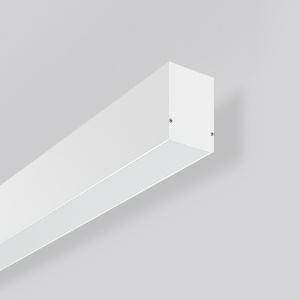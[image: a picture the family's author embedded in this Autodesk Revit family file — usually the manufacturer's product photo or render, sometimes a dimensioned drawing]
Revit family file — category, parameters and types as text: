
# Revit family: less_is_more_50_312606_002_e624
name_source: partatom
category: Lighting Fixtures
units: mm (PartAtom-declared; Revit-internal decimal feet)

## family parameters
Cut with Voids When Loaded = No
Host = Face
Light Source = No
Part Type = Normal
Room Calculation Point = No
Round Connector Dimension = Use Diameter
Shared = No

## types (1)
- LESS IS MORE 50 (1 x LED Modul 830, 1950 lm, 3000)
    Apparent Load = 15 VA
    CIE Flux Codes = 48 80 96 50 100
    Color Rendering = 80
    Color Temperature = 3000
    Default Elevation = 1800 mm
    Description = Series: LESS IS MORE 50
Linear wall luminaires. Housing: extruded aluminium profile, powder-coated. End cap aluminium powder-coated. Diffuser made of non-yellowing plastic (PMMA), opal. Direct 50%, indirect 50% light emission. Suitable for Wall (surface). LED unit with integrated converter interchangeable and removable. Suitable for through-wiring. With sensors or as a safety luminaire on request. 
Colour: traffic white, matt (RAL 9016)
Length: 847 mm
Width: 67 mm
Height: 75 mm
Lamp: LED
Socket: without socket
Colour temperature: 3000K
Colour rendering index (CRI): 80
Light source: LED
Socket lamp2: Without base
Colour temperature: 3000K
Colour rendering index (CRI) 2: 80
System power: 15 W
Rated luminous flux: 1950 lm
Luminous efficiency: 130 lm/W
Control gear: Regulated power supply
Control gear: Regulated power supply
Protection class: I
Type of protection: IP 20
    Height = 75 mm
    Lamp = 1 x LED Modul 830
    Lamp Light Flux = 1950 lm
    Lamp count = 1
    Length = 847 mm
    Lifetime = 50000 h
    Luminous efficacy = 130 lm/W
    Manufacturer = RZB
    ModVariant = No
    Model = 312606.002
    Mounting Place = Wall
    Mounting Type = Surface mounted
    Number of Poles = 1
    OnlyDefault = Yes
    Power Factor = 1
    Product Name = LESS IS MORE 50
    Product group = Surface mounted LED linear luminaires
    ProductGroupID = 2007
    Protection Class = Protection class I
    Protection Degree = IP 20
    RLX_Detail_Level = 1
    RLX_Emergency_Light_Flux = 0 lm
    RLX_Emergency_Type = 0
    RLX_Emergency_Type_DB = No
    RlxData = <blob elided: 39593 chars, md5=09f5c171>
    Socket = socket
    Standby Power = 0 W
    System Light Flux = 1950 lm
    System Power = 15 W
    Type Comments = Product without accessories
    Type Image = 312606.002.jpg
    URL = http://relux.com
    VarID = ---
    Voltage = 0 V
    Weight = 0.00 kg
    Width = 67 mm

## geometry (parser evidence)
native form markers: Blend x4, Sweep x12
no freeform markers — native parametric forms only
